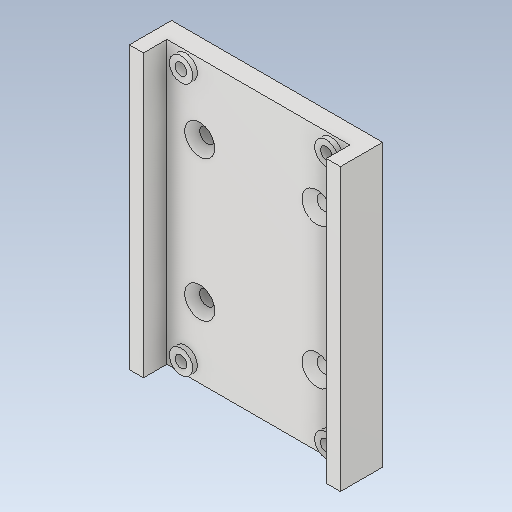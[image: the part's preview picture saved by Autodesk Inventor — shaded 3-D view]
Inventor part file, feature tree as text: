
AUTODESK INVENTOR PART (.ipt)
format: ipt  version: 2020.5 (Build 245400000, 400)  size: 189,440 bytes
history: native  units: mm
features: extrude x5, sketch x5, other x1, chamfer x1
ambient origin geometry x8: Origin, YZ Plane, XZ Plane, XY Plane, X Axis, Y Axis, Z Axis, Center Point
bodies: Body1 (feature_tree)
feature tree (12):
  other  "솔리드1"
  extrude  "돌출1"  Depth=45.0mm
  extrude  "돌출2"  Depth=60.0mm
  extrude  "돌출3"  Depth=30.0mm
  extrude  "돌출4"  Depth=22.5mm
  extrude  "돌출5"  Depth=4.0mm TaperAngle=0.0deg
  chamfer  "모따기1"  Distance=31.0mm
  sketch  "스케치1"
  sketch  "스케치2"
  sketch  "스케치3"
  sketch  "스케치4"
  sketch  "스케치5"
